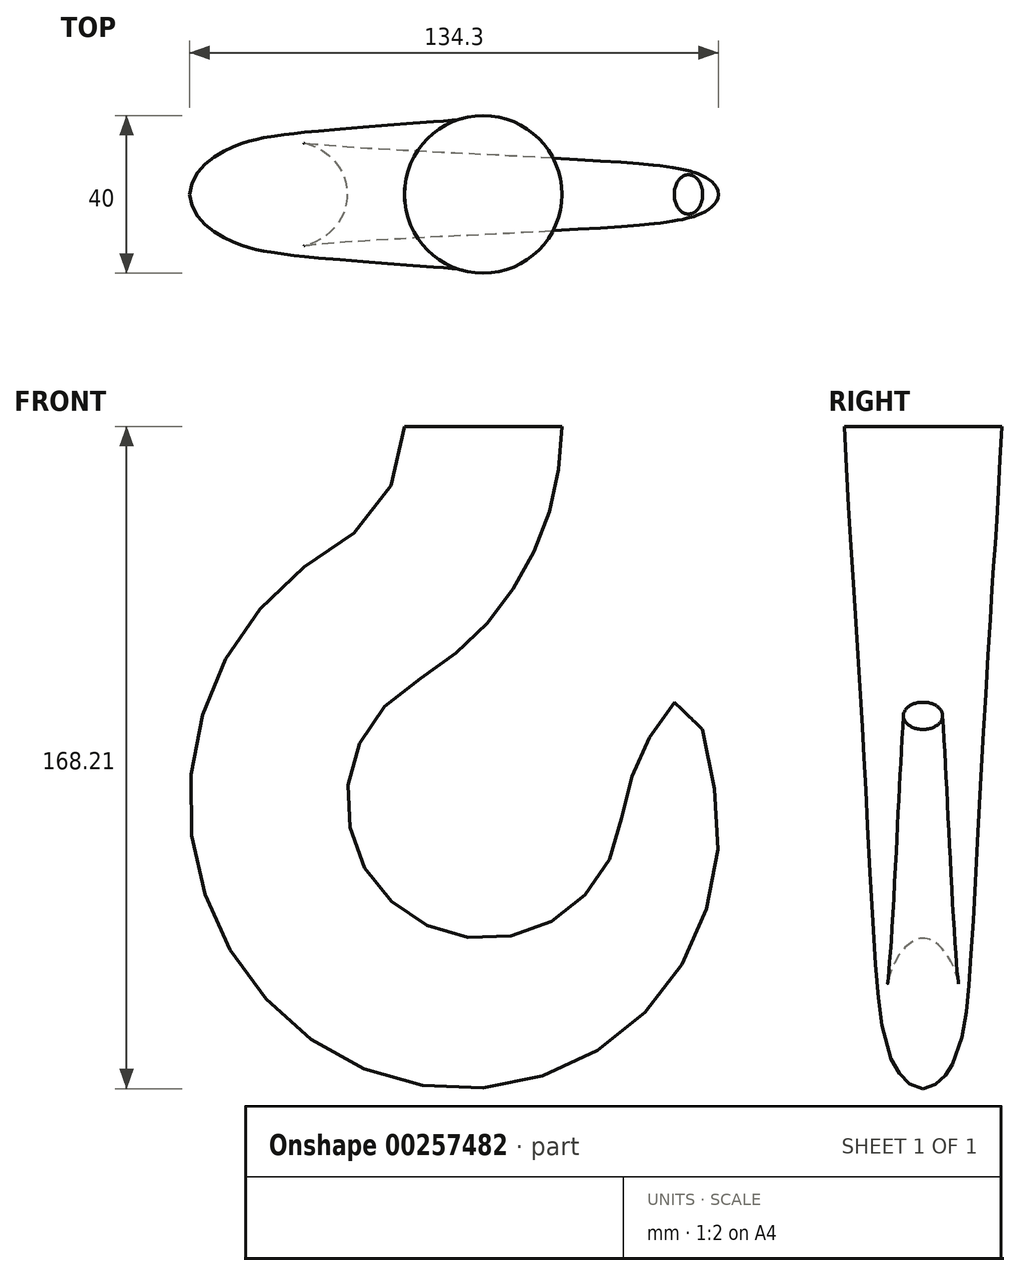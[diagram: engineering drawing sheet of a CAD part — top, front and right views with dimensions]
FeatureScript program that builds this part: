
annotation { "Feature Type Name" : "Feature", "Feature Type Description" : "" }
export const myFeature = defineFeature(function(context is Context, id is Id, definition is map)
    precondition{}
    {
        {
            var Q0;
            Q0=qCreatedBy(makeId("Front.planeOp"),FACE);
            var sketch = newSketch(context, id + "F0", { "sketchPlane" : qUnion([Q0])});
            skLineSegment(sketch, "E0", {"start": v(0, 0) * mm, "end": v(-40, 0) * mm});
            skLineSegment(sketch, "E1", {"start": v(-143.54, -95) * mm, "end": v(113.77, -95) * mm, "construction": true});
            skLineSegment(sketch, "E2", {"start": v(-20, 0) * mm, "end": v(-20, -168) * mm, "construction": true});
            skArc(sketch, "E3", {"start": v(-40, 0) * mm, "mid": v(-44.65, -17.43) * mm, "end": v(-57.36, -30.23) * mm});
            skArc(sketch, "E4", {"start": v(-62.34, -156.6) * mm, "mid": v(-94.49, -92.04) * mm, "end": v(-57.36, -30.23) * mm});
            skArc(sketch, "E5", {"start": v(0, 0) * mm, "mid": v(-9.96, -37.35) * mm, "end": v(-37.2, -64.77) * mm});
            skArc(sketch, "E6", {"start": v(-37.2, -64.77) * mm, "mid": v(-39.11, -124.02) * mm, "end": v(15.1, -100.02) * mm});
            skArc(sketch, "E7", {"start": v(37.4, -85.89) * mm, "mid": v(12.34, -156.24) * mm, "end": v(-62.34, -156.6) * mm});
            skArc(sketch, "E8", {"start": v(37.4, -85.89) * mm, "mid": v(36.38, -81.45) * mm, "end": v(35.78, -76.93) * mm});
            skLineSegment(sketch, "E9", {"start": v(35.78, -76.93) * mm, "end": v(28.54, -70.02) * mm});
            skArc(sketch, "E10", {"start": v(28.54, -70.02) * mm, "mid": v(19.72, -84.09) * mm, "end": v(15.1, -100.02) * mm});
            skSolve(sketch);
        }
        {
            var Q0;
            Q0=qCreatedBy(makeId("Top.planeOp"),FACE);
            var sketch = newSketch(context, id + "F1", { "sketchPlane" : qUnion([Q0])});
            skPoint(sketch, "E11.0", {"position": v(-40, 0) * mm});
            skPoint(sketch, "E12.0", {"position": v(0, 0) * mm});
            skLineSegment(sketch, "E13.0", {"start": v(0, 0) * mm, "end": v(-40, 0) * mm, "construction": true});
            skCircle(sketch, "E14", {"center": v(-20, 0) * mm, "radius": 20 * mm});
            skSolve(sketch);
        }
        {
            var Q0;
            Q0=sQuery(id+"F0.wireOp",EDGE,"E9");
            cPlane(context, id + "F2", {"entities" : qUnion([Q0]), "cplaneType" : CPlaneType.LINE_ANGLE, "offset" : 25 * mm, "angle" : 90 * degree, "width" : 150 * mm, "height" : 150 * mm});
        }
        {
            var Q0;
            Q0=qCreatedBy(id+"F2.planeOp",FACE);
            var sketch = newSketch(context, id + "F3", { "sketchPlane" : qUnion([Q0])});
            skPoint(sketch, "E15.0", {"position": v(69, 0) * mm});
            skLineSegment(sketch, "E16.0", {"start": v(79, 0) * mm, "end": v(69, 0) * mm, "construction": true});
            skCircle(sketch, "E17", {"center": v(74, 0) * mm, "radius": 5 * mm});
            skSolve(sketch);
        }
        {
            var Q0;
            Q0=qCreatedBy(makeId("Front.planeOp"),FACE);
            var sketch = newSketch(context, id + "F4", { "sketchPlane" : qUnion([Q0])});
            skArc(sketch, "E18.0", {"start": v(-40, 0) * mm, "mid": v(-44.65, -17.43) * mm, "end": v(-57.36, -30.23) * mm});
            skArc(sketch, "E19.0", {"start": v(-62.34, -156.6) * mm, "mid": v(-94.49, -92.04) * mm, "end": v(-57.36, -30.23) * mm});
            skArc(sketch, "E20.0", {"start": v(37.4, -85.89) * mm, "mid": v(12.34, -156.24) * mm, "end": v(-62.34, -156.6) * mm});
            skArc(sketch, "E21.0", {"start": v(37.4, -85.89) * mm, "mid": v(36.38, -81.45) * mm, "end": v(35.78, -76.93) * mm});
            skSolve(sketch);
        }
        {
            var Q0;
            Q0=qCreatedBy(makeId("Front.planeOp"),FACE);
            var sketch = newSketch(context, id + "F5", { "sketchPlane" : qUnion([Q0])});
            skArc(sketch, "E22.0", {"start": v(0, 0) * mm, "mid": v(-9.96, -37.35) * mm, "end": v(-37.2, -64.77) * mm});
            skArc(sketch, "E23.0", {"start": v(-37.2, -64.77) * mm, "mid": v(-39.11, -124.02) * mm, "end": v(15.1, -100.02) * mm});
            skArc(sketch, "E24.0", {"start": v(28.54, -70.02) * mm, "mid": v(19.72, -84.09) * mm, "end": v(15.1, -100.02) * mm});
            skSolve(sketch);
        }
        {
            var Q0;
            Q0=makeQuery(id+"F1.imprint","IMPRINT",FACE,{"disambiguationData":[TD([[makeQuery(id+"F1.imprint","IMPRINT",EDGE,{"derivedFrom":sQuery(id+"F1.wireOp",EDGE,"E14")}),1.0]])]});
            var Q1;
            Q1=makeQuery(id+"F3.imprint","IMPRINT",FACE,{"disambiguationData":[TD([[makeQuery(id+"F3.imprint","IMPRINT",EDGE,{"derivedFrom":sQuery(id+"F3.wireOp",EDGE,"E17")}),1.0]])]});
            var Q2;
            Q2 = qConstructionFilter(qBodyType(qCreatedBy(id + "F4" ,EDGE), BodyType.WIRE), ConstructionObject.NO);
            var Q3;
            Q3 = qConstructionFilter(qBodyType(qCreatedBy(id + "F5" ,EDGE), BodyType.WIRE), ConstructionObject.NO);
            loft(context, id + "F6", {"addGuides" : true, "sheetProfilesArray" : [{ "sheetProfileEntities" : qUnion([Q0]) }, { "sheetProfileEntities" : qUnion([Q1]) }], "guidesArray" : [{ "guideEntities" : qUnion([Q2]), "guideDerivativeType" : LoftGuideDerivativeType.DEFAULT, "guideDerivativeMagnitude" : 1 }, { "guideEntities" : qUnion([Q3]), "guideDerivativeType" : LoftGuideDerivativeType.DEFAULT, "guideDerivativeMagnitude" : 1 }]});
        }
    });
